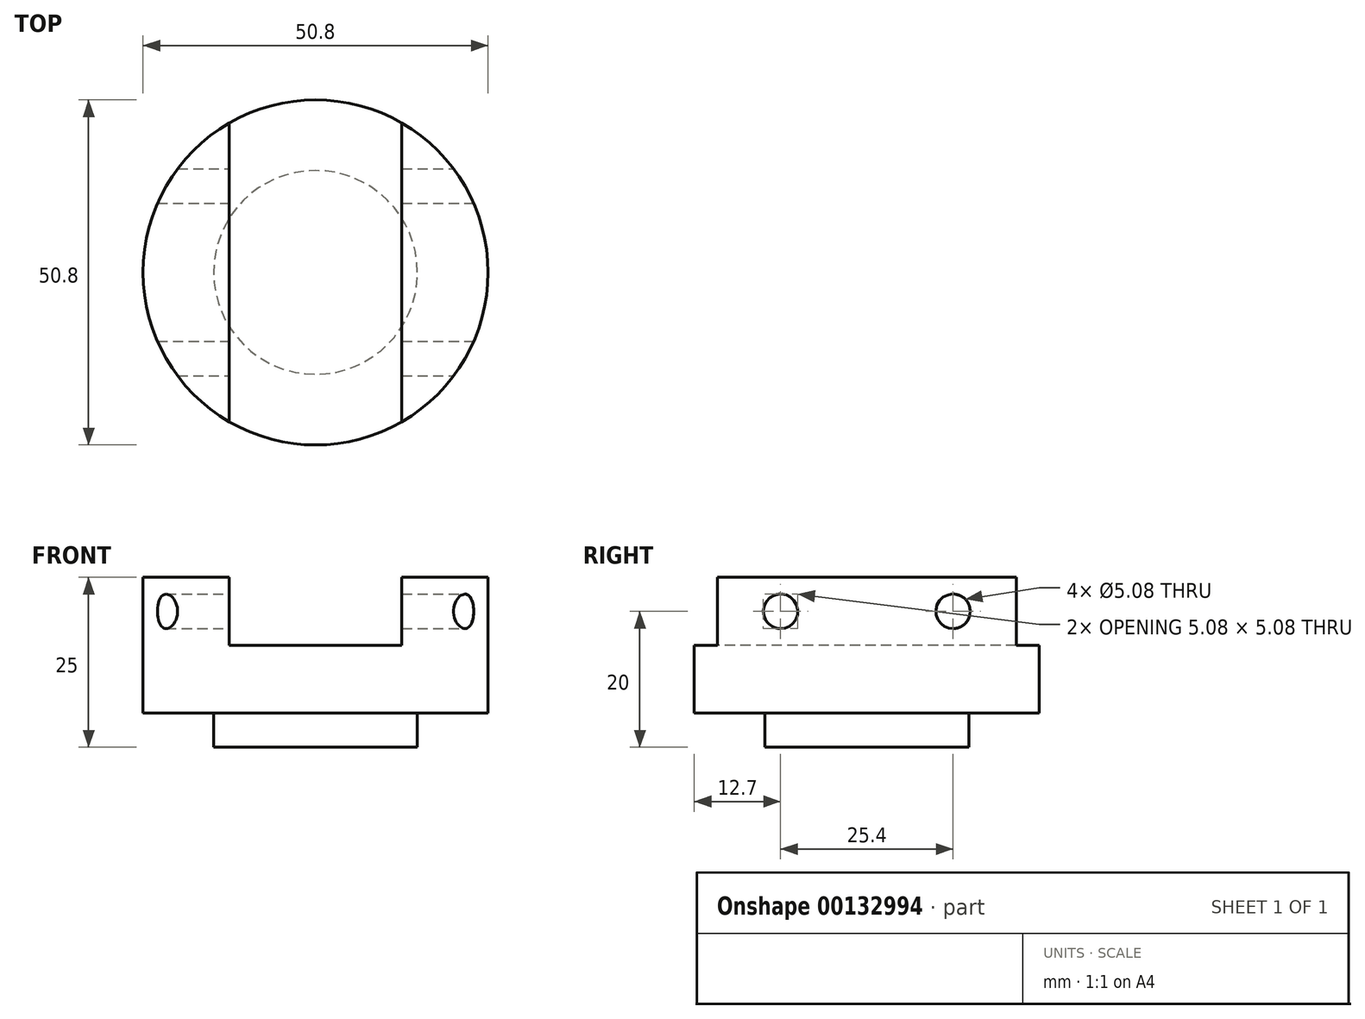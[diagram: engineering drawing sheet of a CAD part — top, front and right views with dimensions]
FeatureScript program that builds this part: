
annotation { "Feature Type Name" : "Feature", "Feature Type Description" : "" }
export const myFeature = defineFeature(function(context is Context, id is Id, definition is map)
    precondition{}
    {
        {
            var Q0;
            Q0=qCreatedBy(makeId("Top.planeOp"),FACE);
            var sketch = newSketch(context, id + "F0", { "sketchPlane" : qUnion([Q0])});
            skCircle(sketch, "E0", {"center": v(0, 0) * mm, "radius": 25.4 * mm});
            skSolve(sketch);
        }
        {
            var Q0;
            Q0 = qSketchRegion(id + "F0", true);
            extrude(context, id + "F1", {"entities" : qUnion([Q0]), "depth" : 20 * mm});
        }
        {
            var Q0;
            Q0=makeQuery(id+"F1.opExtrude","CAP_FACE",FACE,{"disambiguationData":[OSD([sQuery(id+"F0.wireOp",EDGE,"E0")])],"isStart":false});
            var sketch = newSketch(context, id + "F2", { "sketchPlane" : qUnion([Q0])});
            skLineSegment(sketch, "E1.bottom", {"start": v(-12.7, 26.95) * mm, "end": v(12.7, 26.95) * mm});
            skLineSegment(sketch, "E1.top", {"start": v(-12.7, -28.26) * mm, "end": v(12.7, -28.26) * mm});
            skLineSegment(sketch, "E1.left", {"start": v(-12.7, 26.95) * mm, "end": v(-12.7, -28.26) * mm});
            skLineSegment(sketch, "E1.right", {"start": v(12.7, 26.95) * mm, "end": v(12.7, -28.26) * mm});
            skSolve(sketch);
        }
        {
            var Q0;
            Q0 = qSketchRegion(id + "F2", true);
            extrude(context, id + "F3", {"entities" : qUnion([Q0]), "operationType" : NewBodyOperationType.REMOVE, "oppositeDirection" : true, "depth" : 10 * mm});
        }
        {
            var Q0;
            Q0=qCreatedBy(makeId("Right.planeOp"),FACE);
            var sketch = newSketch(context, id + "F4", { "sketchPlane" : qUnion([Q0])});
            skCircle(sketch, "E2", {"center": v(-12.7, 15) * mm, "radius": 2.54 * mm});
            skCircle(sketch, "E3", {"center": v(12.7, 15) * mm, "radius": 2.54 * mm});
            skSolve(sketch);
        }
        {
            var Q0;
            Q0 = qSketchRegion(id + "F4", true);
            extrude(context, id + "F5", {"entities" : qUnion([Q0]), "operationType" : NewBodyOperationType.REMOVE, "oppositeDirection" : true, "depth" : 25.4 * mm, "hasSecondDirection" : true, "secondDirectionOppositeDirection" : false, "secondDirectionDepth" : 25.4 * mm});
        }
        {
            var Q0;
            Q0=makeQuery(id+"F3.boolean.opBoolean","COPY",FACE,{"derivedFrom":makeQuery(id+"F3.opExtrude","CAP_FACE",FACE,{"disambiguationData":[OSD([sQuery(id+"F2.wireOp",EDGE,"E1.bottom"),sQuery(id+"F2.wireOp",EDGE,"E1.top"),sQuery(id+"F2.wireOp",EDGE,"E1.left"),sQuery(id+"F2.wireOp",EDGE,"E1.right")])],"isStart":false})});
            var sketch = newSketch(context, id + "F6", { "sketchPlane" : qUnion([Q0])});
            skCircle(sketch, "E4", {"center": v(0, 0) * mm, "radius": 15 * mm});
            skSolve(sketch);
        }
        {
            var Q0;
            Q0 = qSketchRegion(id + "F6", true);
            extrude(context, id + "F7", {"entities" : qUnion([Q0]), "operationType" : NewBodyOperationType.ADD, "oppositeDirection" : true, "depth" : 15 * mm});
        }
    });
